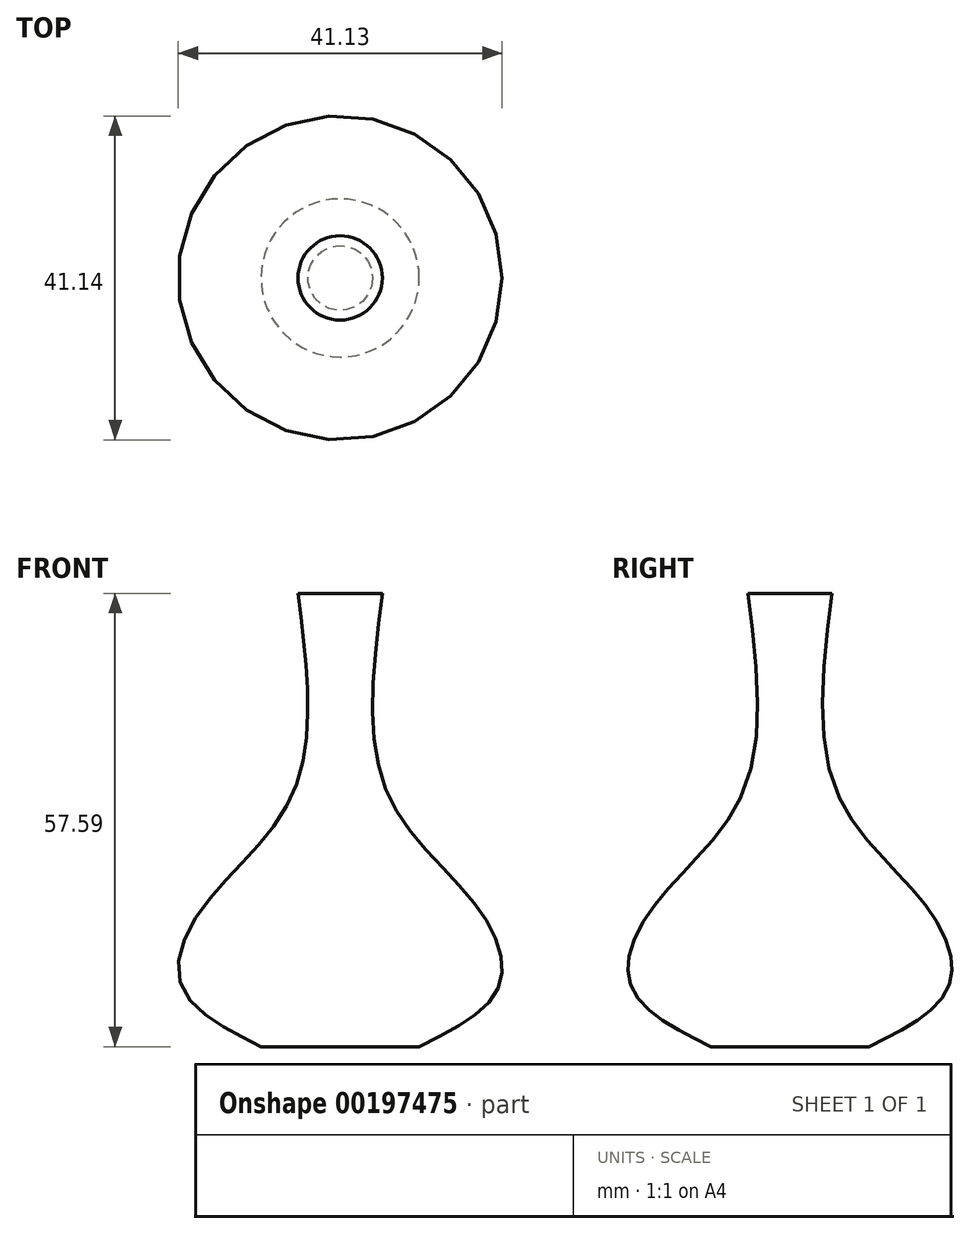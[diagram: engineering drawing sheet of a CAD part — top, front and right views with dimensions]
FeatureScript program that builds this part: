
annotation { "Feature Type Name" : "Feature", "Feature Type Description" : "" }
export const myFeature = defineFeature(function(context is Context, id is Id, definition is map)
    precondition{}
    {
        {
            var Q0;
            Q0=qCreatedBy(makeId("Front.planeOp"),FACE);
            var sketch = newSketch(context, id + "F0", { "sketchPlane" : qUnion([Q0])});
            skFitSpline(sketch, "E0", {"points": [v(5.36, 50.11) * mm, v(6.03, 24.67) * mm, v(17.63, 9.93) * mm, v(20.09, 0) * mm, v(10.04, -7.48) * mm], "startDerivative": vector(-11.23, -88.84) * mm, "endDerivative": vector(-59.32, -29.53) * mm});
            skLineSegment(sketch, "E1", {"start": v(0, 55.03) * mm, "end": v(0, -19.72) * mm, "construction": true});
            skLineSegment(sketch, "E2", {"start": v(10.04, -7.48) * mm, "end": v(0, -7.48) * mm});
            skLineSegment(sketch, "E3", {"start": v(5.36, 50.11) * mm, "end": v(0, 50.11) * mm});
            skLineSegment(sketch, "E4", {"start": v(0, 50.11) * mm, "end": v(0, -7.48) * mm});
            skSolve(sketch);
        }
        {
            var Q0;
            Q0=makeQuery(id+"F0.imprint","IMPRINT",FACE,{"disambiguationData":[TD([[makeQuery(id+"F0.imprint","IMPRINT",EDGE,{"derivedFrom":sQuery(id+"F0.wireOp",EDGE,"E0")}),-1.0]])]});
            var Q1;
            Q1=sQuery(id+"F0.wireOp",EDGE,"E1");
            revolve(context, id + "F1", {"entities" : qUnion([Q0]), "axis" : qUnion([Q1]), "revolveType" : RevolveType.FULL});
        }
    });
